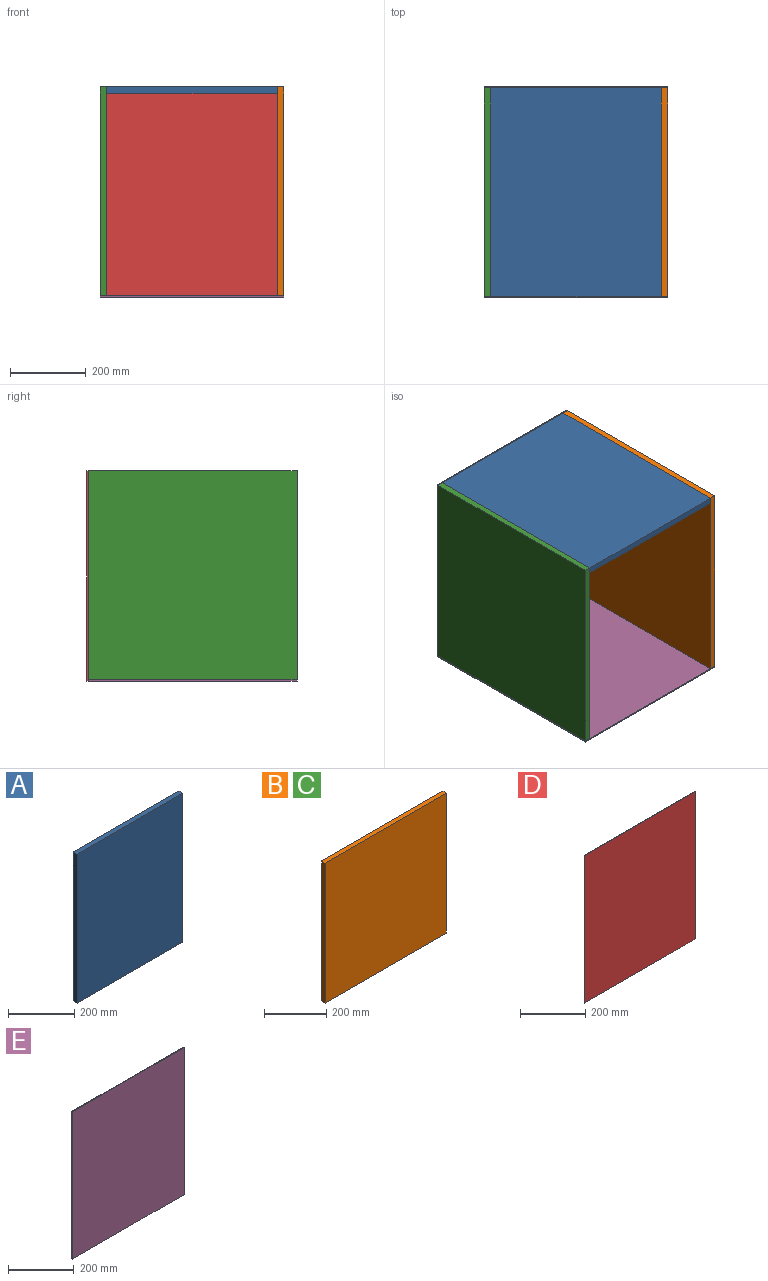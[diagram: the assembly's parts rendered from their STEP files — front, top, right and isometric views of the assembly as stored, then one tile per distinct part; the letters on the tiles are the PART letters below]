
ASSEMBLY  parts=5 mates=4
PART A: 6 faces, bbox 450x16x550 mm
  f0: plane 450x16mm, normal (0,0,1), area 7200mm2, adj f1,f3,f4,f5
  f1: plane 550x16mm, normal (-1,0,0), area 8800mm2, adj f0,f2,f4,f5
  f2: plane 450x16mm, normal (0,0,-1), area 7200mm2, adj f1,f3,f4,f5
  f3: plane 550x16mm, normal (1,0,0), area 8800mm2, adj f0,f2,f4,f5
  f4: plane 550x450mm, normal (0,-1,0), area 247500mm2, adj f0,f1,f2,f3
  f5: plane 550x450mm, normal (0,1,0), area 247500mm2, adj f0,f1,f2,f3
PART B: 6 faces, bbox 550x16x550 mm
  f0: plane 550x16mm, normal (0,0,1), area 8800mm2, adj f1,f3,f4,f5
  f1: plane 550x16mm, normal (-1,0,0), area 8800mm2, adj f0,f2,f4,f5
  f2: plane 550x16mm, normal (0,0,-1), area 8800mm2, adj f1,f3,f4,f5
  f3: plane 550x16mm, normal (1,0,0), area 8800mm2, adj f0,f2,f4,f5
  f4: plane 550x550mm, normal (0,-1,0), area 302500mm2, adj f0,f1,f2,f3
  f5: plane 550x550mm, normal (0,1,0), area 302500mm2, adj f0,f1,f2,f3
PART C: same geometry as B
PART D: 6 faces, bbox 482x3x553 mm
  f0: plane 482x3mm, normal (0,0,1), area 1446mm2, adj f1,f3,f4,f5
  f1: plane 553x3mm, normal (-1,0,0), area 1659mm2, adj f0,f2,f4,f5
  f2: plane 482x3mm, normal (0,0,-1), area 1446mm2, adj f1,f3,f4,f5
  f3: plane 553x3mm, normal (1,0,0), area 1659mm2, adj f0,f2,f4,f5
  f4: plane 553x482mm, normal (0,-1,0), area 266546mm2, adj f0,f1,f2,f3
  f5: plane 553x482mm, normal (0,1,0), area 266546mm2, adj f0,f1,f2,f3
PART E: 6 faces, bbox 482x3x550 mm
  f0: plane 482x3mm, normal (0,0,1), area 1446mm2, adj f1,f3,f4,f5
  f1: plane 550x3mm, normal (-1,0,0), area 1650mm2, adj f0,f2,f4,f5
  f2: plane 482x3mm, normal (0,0,-1), area 1446mm2, adj f1,f3,f4,f5
  f3: plane 550x3mm, normal (1,0,0), area 1650mm2, adj f0,f2,f4,f5
  f4: plane 550x482mm, normal (0,-1,0), area 265100mm2, adj f0,f1,f2,f3
  f5: plane 550x482mm, normal (0,1,0), area 265100mm2, adj f0,f1,f2,f3
PLACE A rot(axis=(-1,0,0),90deg) t=(-241.97,-197.25,-32.26)mm
PLACE B rot(axis=(0.71,-0.71,0),180deg) t=(-53.89,-66.9,-202.83)mm
PLACE C rot(axis=(0.71,-0.71,0),180deg) t=(-519.89,-66.9,-202.83)mm
PLACE D t=(-257.97,162.36,-385.37)mm
PLACE E rot(axis=(1,0,0),90deg) t=(-257.97,-31.02,-575.76)mm
MATE fastened A.f4 <-> B.f2  axis (0,0,1) through (-61.89,160.86,-24.26)mm
MATE fastened C.f4 <-> A.f1  axis (1,0,0) through (-511.89,-389.14,-24.26)mm
MATE fastened D.f4 <-> E.f2  axis (0,-1,0) through (-45.89,160.86,-577.26)mm
MATE fastened B.f0 <-> E.f5  axis (0,0,-1) through (-45.89,-389.14,-574.26)mm
